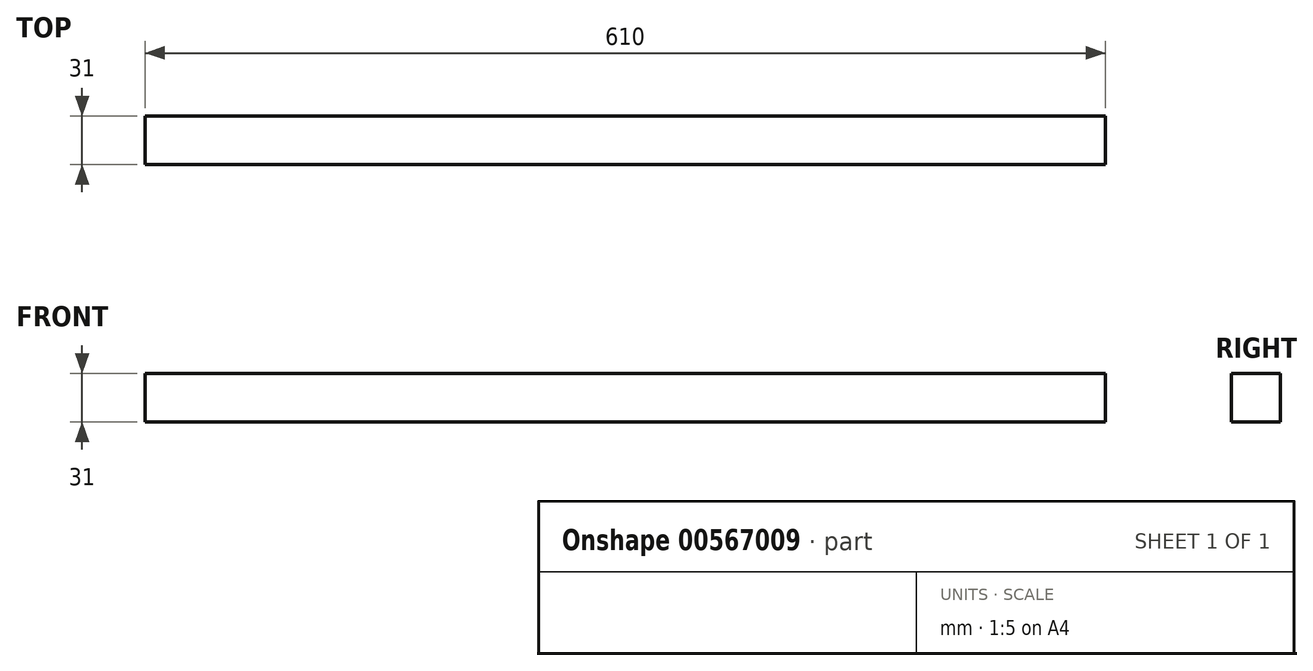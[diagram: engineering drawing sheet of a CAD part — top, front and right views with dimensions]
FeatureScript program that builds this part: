
annotation { "Feature Type Name" : "Feature", "Feature Type Description" : "" }
export const myFeature = defineFeature(function(context is Context, id is Id, definition is map)
    precondition{}
    {
        {
            var Q0;
            Q0=qCreatedBy(makeId("Front.planeOp"),FACE);
            var sketch = newSketch(context, id + "F0", { "sketchPlane" : qUnion([Q0])});
            skLineSegment(sketch, "E0.bottom", {"start": v(-65.04, 71.82) * mm, "end": v(544.96, 71.82) * mm});
            skLineSegment(sketch, "E0.top", {"start": v(-65.04, 40.82) * mm, "end": v(544.96, 40.82) * mm});
            skLineSegment(sketch, "E0.left", {"start": v(-65.04, 71.82) * mm, "end": v(-65.04, 40.82) * mm});
            skLineSegment(sketch, "E0.right", {"start": v(544.96, 71.82) * mm, "end": v(544.96, 40.82) * mm});
            skSolve(sketch);
        }
        {
            var Q0;
            Q0 = qSketchRegion(id + "F0", true);
            extrude(context, id + "F1", {"entities" : qUnion([Q0]), "depth" : 31 * mm, "offsetDistance" : 25 * mm});
        }
    });
